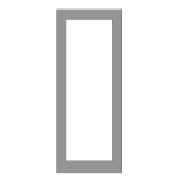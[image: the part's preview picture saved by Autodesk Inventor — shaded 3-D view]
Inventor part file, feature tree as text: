
AUTODESK INVENTOR PART (.ipt)
format: ipt  version: 2022.2 (Build 262287000, 287)  size: 146,432 bytes
history: native  units: in
note: dims shown in document units (in); Inventor stores cm internally (conversion verified against a paired STEP export)
features: sketch x5, other x4, hole x1, plane x1
ambient origin geometry x8: Origin, YZ Plane, XZ Plane, XY Plane, X Axis, Y Axis, Z Axis, Center Point
bodies: Solid1 (feature_tree), Body (feature_tree)
feature tree (11):
  other  "Driven Length"
  other  "Frame Generator"
  other  "Start Plane"
  other  "End Plane"
  sketch  "Sketch8"  dims[d3=0.125in]
  hole  "Hole1"  [1 undecoded]
  sketch  "Sketch"  dims[d7=20.0in d8=0.13in d9=0.0in d14=90.0deg d11=20.0in d16=0.25in d17=1.0in d18=1.0in d19=0.25in d20=1.0in d21=1.0in d22=0.1695in d23=0.75in d24=0.375in d25=0.06in d26=0.5635in d27=2.0in d28=0.8108in]
  sketch  "Sketch6"  dims[d0=1.0in d1=2.0in]
  plane  "Work Plane5"
  sketch  "Sketch7"  dims[d2=0.125in]
  sketch  "Sketch9"  dims[d6=-0.0in]
note: 1 required parameter value undecoded (feature->parameter linkage not recoverable at this tier; creation-order binding heuristic only, values carry confidence <= 0.55)
